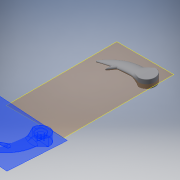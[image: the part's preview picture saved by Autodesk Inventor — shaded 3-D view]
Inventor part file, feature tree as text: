
AUTODESK INVENTOR PART (.ipt)
format: ipt  version: 2019 (Build 230136000, 136)  size: 421,888 bytes
history: native  units: mm
features: other x9, sketch x9, extrude x4, fillet x4, loft x2, revolve x1
ambient origin geometry x8: Origin, YZ Plane, XZ Plane, XY Plane, X Axis, Y Axis, Z Axis, Center Point
bodies: Body1 (feature_tree)
feature tree (29):
  other  "Твердое тело1"
  extrude  "Выдавливание1"  Depth=20.0mm TaperAngle=0.0deg
  other  "РабПлоскость5"
  loft  "Лофт3"
  other  "РабПлоскость6"
  sketch  "Эскиз11"
  revolve  "Вращение2"
  other  "РабПлоскость7"
  sketch  "Эскиз13"
  other  "РабПлоскость8"
  loft  "Лофт4"
  extrude  "Выдавливание3"  Depth=20.0mm
  extrude  "Выдавливание4"  TaperAngle=0.0deg  [1 undecoded]
  fillet  "Сопряжение2"  [1 undecoded]
  fillet  "Сопряжение3"  [1 undecoded]
  other  "РабПлоскость9"
  extrude  "Выдавливание5"  Depth=115.0mm
  fillet  "Сопряжение5"  Radius=3.333333mm
  fillet  "Сопряжение6"  Radius=20.0mm
  sketch  "Эскиз1"
  sketch  "Эскиз9"
  sketch  "Эскиз10"
  other  "Ребра4"
  sketch  "Эскиз12"
  sketch  "Эскиз14"
  other  "Ребра5"
  other  "Ребра6"
  sketch  "Эскиз15"
  sketch  "Эскиз16"
note: 3 required parameter values undecoded (feature->parameter linkage not recoverable at this tier; creation-order binding heuristic only, values carry confidence <= 0.55)
